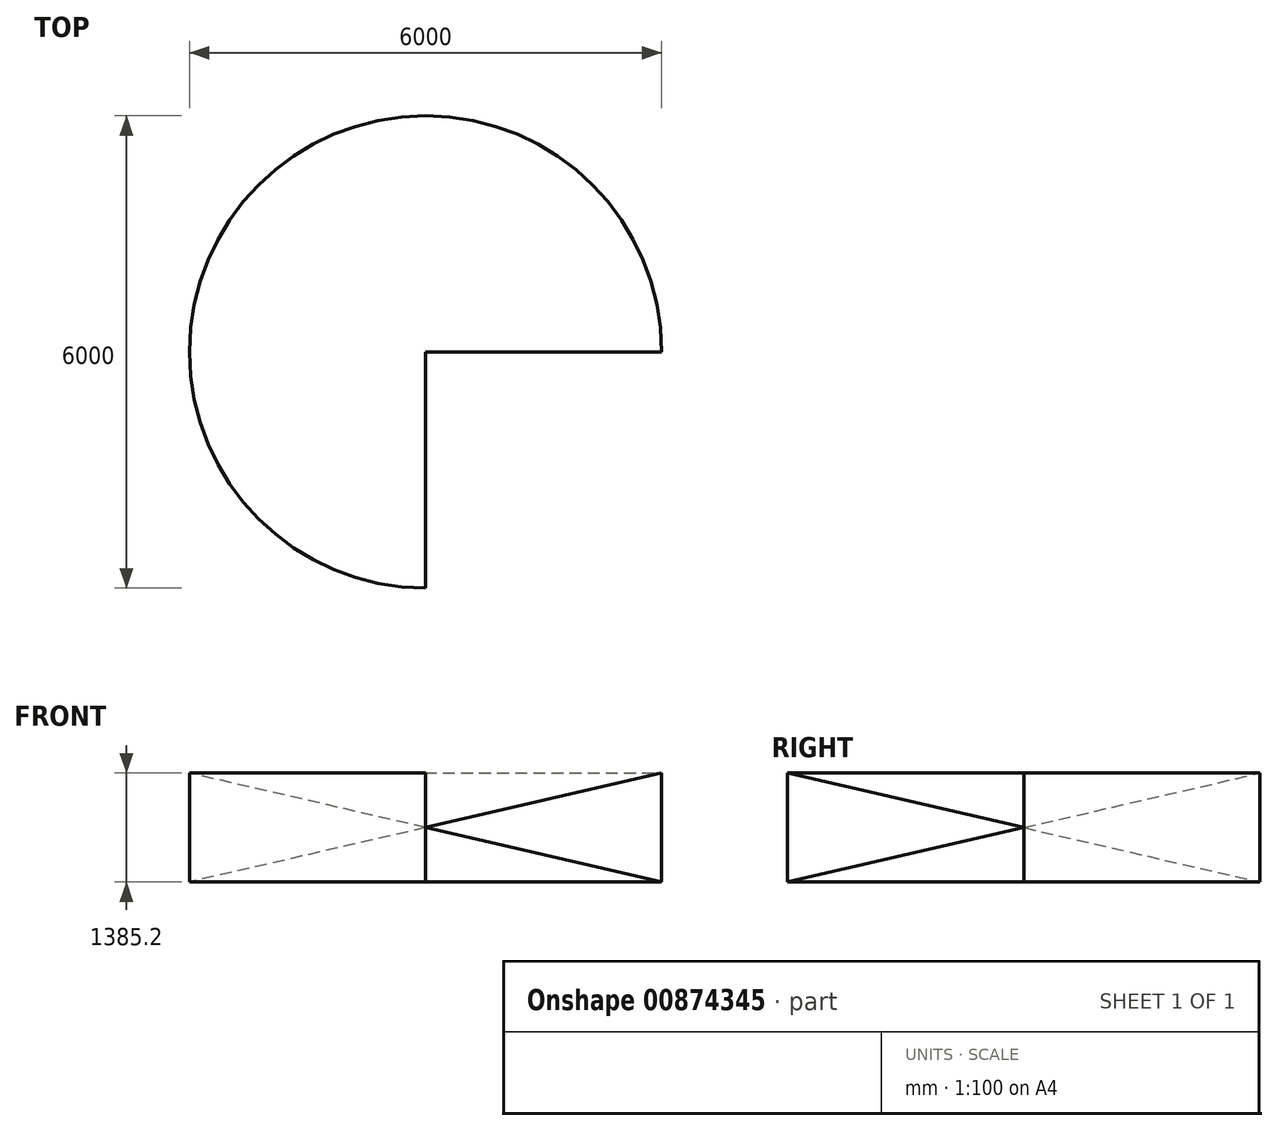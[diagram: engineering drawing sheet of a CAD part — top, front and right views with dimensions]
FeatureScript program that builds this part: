
annotation { "Feature Type Name" : "Feature", "Feature Type Description" : "" }
export const myFeature = defineFeature(function(context is Context, id is Id, definition is map)
    precondition{}
    {
        {
            var Q0;
            Q0=qCreatedBy(makeId("Front.planeOp"),FACE);
            var sketch = newSketch(context, id + "F0", { "sketchPlane" : qUnion([Q0])});
            skLineSegment(sketch, "E0", {"start": v(0, 0) * mm, "end": v(0, 800) * mm, "construction": true});
            skLineSegment(sketch, "E1", {"start": v(0, 800) * mm, "end": v(3000, 800) * mm, "construction": true});
            skLineSegment(sketch, "E2", {"start": v(0, 800) * mm, "end": v(3000, 107.4) * mm});
            skLineSegment(sketch, "E3.MirrorCS", {"start": v(0, 800) * mm, "end": v(3000, 1492.6) * mm});
            skLineSegment(sketch, "E4", {"start": v(3000, 107.4) * mm, "end": v(3000, 1492.6) * mm});
            skSolve(sketch);
        }
        {
            var Q0;
            Q0 = qSketchRegion(id + "F0", true);
            var Q1;
            Q1=sQuery(id+"F0.wireOp",EDGE,"E0");
            revolve(context, id + "F1", {"surfaceOperationType" : NewSurfaceOperationType.NEW, "entities" : qUnion([Q0]), "axis" : qUnion([Q1]), "revolveType" : RevolveType.ONE_DIRECTION, "angle" : 270 * degree});
        }
    });
